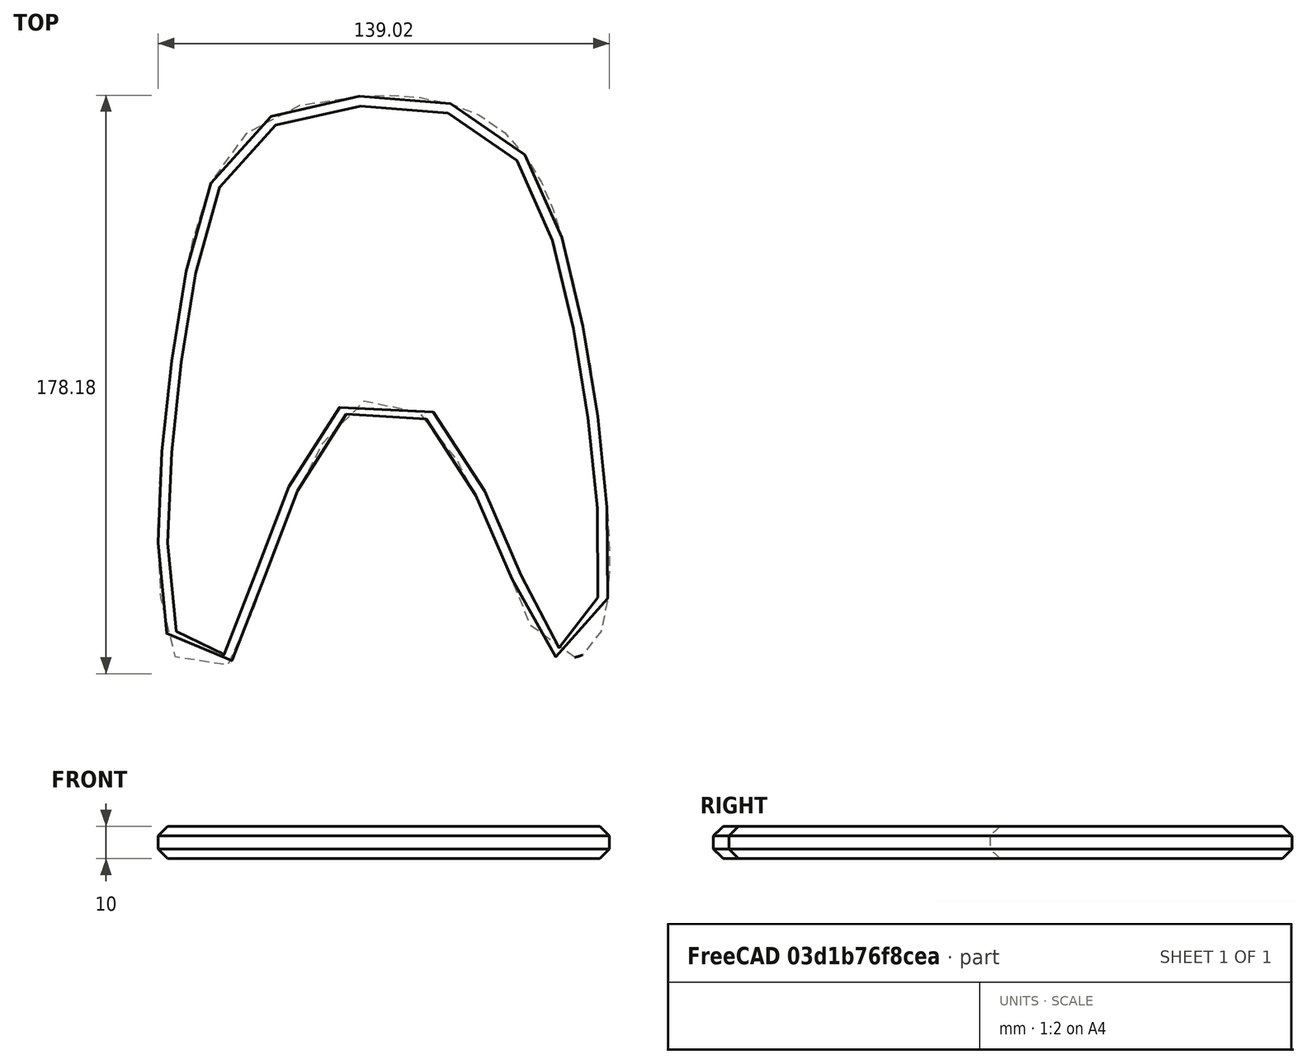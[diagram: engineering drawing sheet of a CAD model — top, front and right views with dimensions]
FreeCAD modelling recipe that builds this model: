
FCSTD DOCUMENT  (FreeCAD 1.0R39285 (Git))
Label: frappe_machine_part
License: All rights reserved
objects: Image::ImagePlane×1, Sketcher::SketchObject×1, PartDesign::Pad×1, PartDesign::Chamfer×1, PartDesign::Body×1
note: 9 computed .brp shape members not serialized (recipe doc carries the construction recipe); baked Part::Feature solids carry a one-line shape summary decoded from their .brp

FEATURE [Image::ImagePlane] _0251004_114848  label="20251004_114848"
  XSize = 190.637
  YSize = 241.193
FEATURE [Sketcher::SketchObject] Sketch
  ArcFitTolerance = 1e-06
  AttachmentSupport = -> [XY_Plane]
  FullyConstrained = false
  MakeInternals = false
  MapMode = 5
  sketch-geometry (103):
    g0-g49: GeomPoint [constr] x50 (B-spline internal-alignment scaffolding for g50; pole/knot coordinates omitted)
    g50: BSplineCurve PolesCount=51 KnotsCount=51 Degree=3 IsPeriodic=1
    g51-g101: Circle [constr] x51 (B-spline internal-alignment scaffolding for g50; pole/knot coordinates omitted)
    g102: GeomPoint [constr] X=-27.0567 Y=90.0824 Z=0
  constraints (104):
    c: InternalAlignment(g0-g49 -> g50) x50
    c: InternalAlignment(g51,g50)
    c: Weight(g51) = 1
    c: InternalAlignment(g52,g50)
    c: Equal(g52,g51)
    c: InternalAlignment(g53,g50)
    c: Equal(g53,g51)
    c: InternalAlignment(g54,g50)
    c: Equal(g54,g51)
    c: InternalAlignment(g55,g50)
    c: Equal(g55,g51)
    c: InternalAlignment(g56,g50)
    c: Equal(g56,g51)
    c: InternalAlignment(g57,g50)
    c: Equal(g57,g51)
    c: InternalAlignment(g58,g50)
    c: Equal(g58,g51)
    c: InternalAlignment(g59,g50)
    c: Equal(g59,g51)
    c: InternalAlignment(g60,g50)
    c: Equal(g60,g51)
    c: InternalAlignment(g61,g50)
    c: Equal(g61,g51)
    c: InternalAlignment(g62,g50)
    c: Equal(g62,g51)
    c: InternalAlignment(g63,g50)
    c: Equal(g63,g51)
    c: InternalAlignment(g64,g50)
    c: Equal(g64,g51)
    c: InternalAlignment(g65,g50)
    c: Equal(g65,g51)
    c: InternalAlignment(g66,g50)
    c: Equal(g66,g51)
    c: InternalAlignment(g67,g50)
    c: Equal(g67,g51)
    c: InternalAlignment(g68,g50)
    c: Equal(g68,g51)
    c: InternalAlignment(g69,g50)
    c: Equal(g69,g51)
    c: InternalAlignment(g70,g50)
    c: Equal(g70,g51)
    c: InternalAlignment(g71,g50)
    c: Equal(g71,g51)
    c: InternalAlignment(g72,g50)
    c: Equal(g72,g51)
    c: InternalAlignment(g73,g50)
    c: Equal(g73,g51)
    c: InternalAlignment(g74,g50)
    c: Equal(g74,g51)
    c: InternalAlignment(g75,g50)
    c: Equal(g75,g51)
    c: InternalAlignment(g76,g50)
    c: Equal(g76,g51)
    c: InternalAlignment(g77,g50)
    c: Equal(g77,g51)
    c: InternalAlignment(g78,g50)
    c: Equal(g78,g51)
    c: InternalAlignment(g79,g50)
    c: Equal(g79,g51)
    c: InternalAlignment(g80,g50)
    c: Equal(g80,g51)
    c: InternalAlignment(g81,g50)
    c: Equal(g81,g51)
    c: InternalAlignment(g82,g50)
    c: Equal(g82,g51)
    c: InternalAlignment(g83,g50)
    c: Equal(g83,g51)
    c: InternalAlignment(g84,g50)
    c: Equal(g84,g51)
    c: InternalAlignment(g85,g50)
    c: Equal(g85,g51)
    c: InternalAlignment(g86,g50)
    c: Equal(g86,g51)
    c: InternalAlignment(g87,g50)
    c: Equal(g87,g51)
    c: InternalAlignment(g88,g50)
    c: Equal(g88,g51)
    c: InternalAlignment(g89,g50)
    c: Equal(g89,g51)
    c: InternalAlignment(g90,g50)
    c: Equal(g90,g51)
    c: InternalAlignment(g91,g50)
    c: Equal(g91,g51)
    c: InternalAlignment(g92,g50)
    c: Equal(g92,g51)
    c: InternalAlignment(g93,g50)
    c: Equal(g93,g51)
    c: InternalAlignment(g94,g50)
    c: Equal(g94,g51)
    c: InternalAlignment(g95,g50)
    c: Equal(g95,g51)
    c: InternalAlignment(g96,g50)
    c: Equal(g96,g51)
    c: InternalAlignment(g97,g50)
    c: Equal(g97,g51)
    c: InternalAlignment(g98,g50)
    c: Equal(g98,g51)
    c: InternalAlignment(g99,g50)
    c: Equal(g99,g51)
    c: InternalAlignment(g100,g50)
    c: Equal(g100,g51)
    c: InternalAlignment(g101,g50)
    c: Equal(g101,g51)
    c: InternalAlignment(g102,g50)
FEATURE [PartDesign::Pad] Pad
  Direction = (0,0,1)
  Length = 10
  Length2 = 10
  Profile = -> Sketch
  ReferenceAxis = -> Sketch [N_Axis]
  Refine = true
  Suppressed = false
  Type = 0
FEATURE [PartDesign::Chamfer] Chamfer
  Angle = 45
  Base = -> Pad [Edge2,Edge3]
  BaseFeature = -> Pad
  ChamferType = 0
  FlipDirection = false
  Refine = true
  Size = 3
  Size2 = 1
  SupportTransform = false
  Suppressed = false
  UseAllEdges = false
FEATURE [PartDesign::Body] Body
  AllowCompound = false
  Group = -> [Sketch,Pad,Chamfer]
  Origin = -> Origin
  Tip = -> Chamfer
